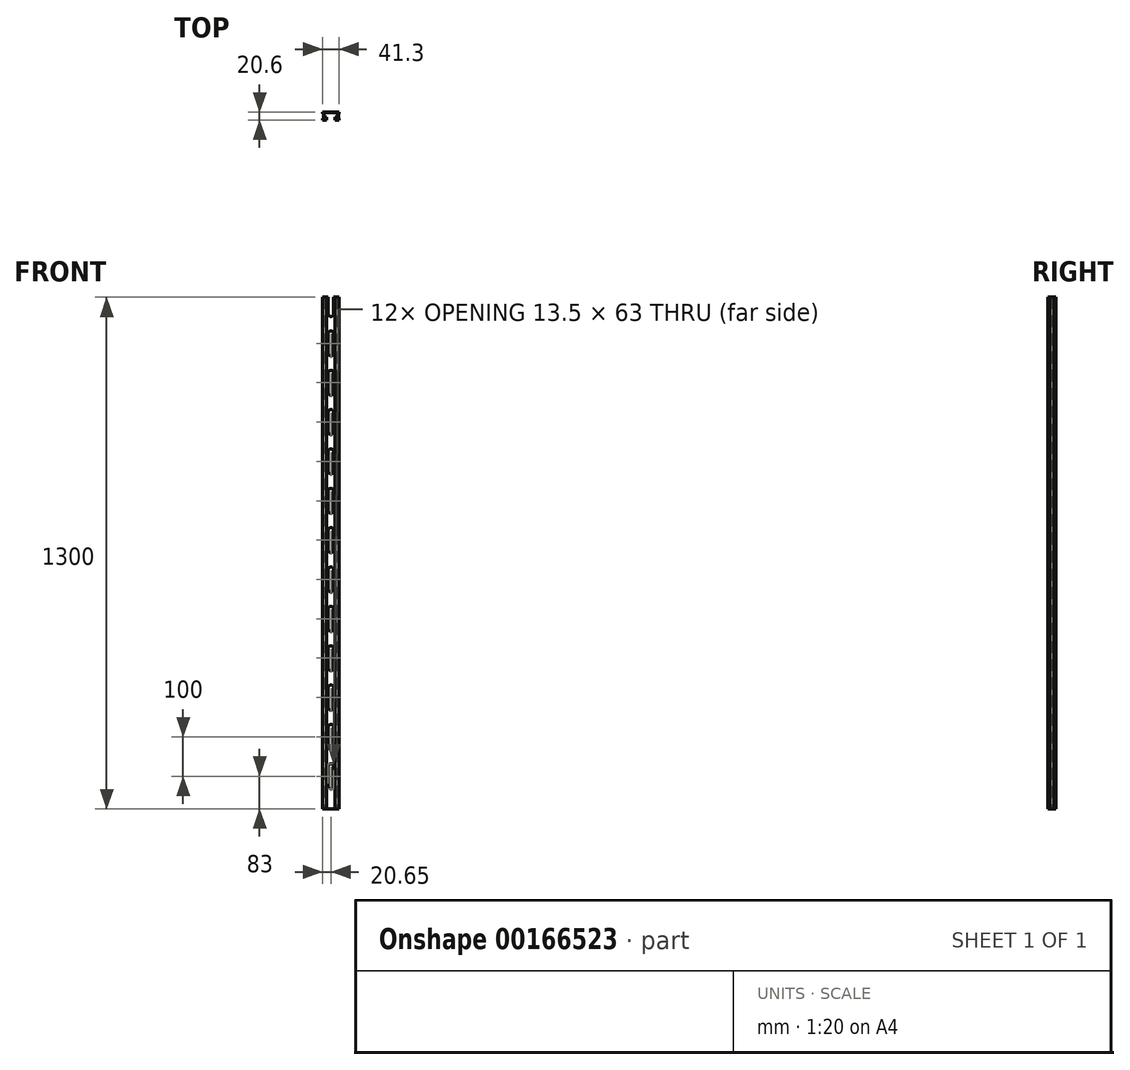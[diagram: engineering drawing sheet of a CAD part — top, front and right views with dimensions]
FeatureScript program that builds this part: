
annotation { "Feature Type Name" : "Feature", "Feature Type Description" : "" }
export const myFeature = defineFeature(function(context is Context, id is Id, definition is map)
    precondition{}
    {
        {
            var Q0;
            Q0=qCreatedBy(makeId("Top.planeOp"),FACE);
            var sketch = newSketch(context, id + "F0", { "sketchPlane" : qUnion([Q0])});
            skPoint(sketch, "E0.middle", {"position": v(0, 0) * mm});
            skLineSegment(sketch, "E1", {"start": v(0, 10.3) * mm, "end": v(-20.65, 10.3) * mm});
            skLineSegment(sketch, "E2", {"start": v(0, 8.3) * mm, "end": v(-18.65, 8.3) * mm});
            skLineSegment(sketch, "E3", {"start": v(-18.65, 8.3) * mm, "end": v(-18.65, 6.8) * mm});
            skLineSegment(sketch, "E4", {"start": v(-18.65, 6.8) * mm, "end": v(-17.15, 6.8) * mm, "construction": true});
            skLineSegment(sketch, "E5", {"start": v(-17.15, 6.8) * mm, "end": v(-17.15, 5.3) * mm, "construction": true});
            skPoint(sketch, "E6.endSnap0", {"position": v(-20.65, 0) * mm});
            skLineSegment(sketch, "E7", {"start": v(-17.15, -5.3) * mm, "end": v(-17.15, -6.8) * mm, "construction": true});
            skLineSegment(sketch, "E8", {"start": v(-17.15, -6.8) * mm, "end": v(-18.65, -6.8) * mm, "construction": true});
            skLineSegment(sketch, "E9", {"start": v(-20.65, 10.3) * mm, "end": v(-20.65, 6.3) * mm});
            skLineSegment(sketch, "E10", {"start": v(-20.65, 6.3) * mm, "end": v(-19.15, 6.3) * mm, "construction": true});
            skLineSegment(sketch, "E11", {"start": v(-20.65, -10.3) * mm, "end": v(-20.65, -6.3) * mm});
            skLineSegment(sketch, "E12", {"start": v(-20.65, -6.3) * mm, "end": v(-19.15, -6.3) * mm, "construction": true});
            skLineSegment(sketch, "E13", {"start": v(-19.15, -6.3) * mm, "end": v(-19.15, -4.8) * mm, "construction": true});
            skLineSegment(sketch, "E14", {"start": v(-19.15, 6.3) * mm, "end": v(-19.15, 4.8) * mm, "construction": true});
            skLineSegment(sketch, "E15", {"start": v(-20.65, 6.3) * mm, "end": v(-19.15, 4.8) * mm});
            skLineSegment(sketch, "E16", {"start": v(-19.15, -4.8) * mm, "end": v(-20.65, -6.3) * mm});
            skLineSegment(sketch, "E17", {"start": v(-19.15, -4.8) * mm, "end": v(-19.15, 4.8) * mm});
            skLineSegment(sketch, "E18", {"start": v(-18.65, -6.8) * mm, "end": v(-17.15, -5.3) * mm});
            skLineSegment(sketch, "E19", {"start": v(-17.15, 5.3) * mm, "end": v(-18.65, 6.8) * mm});
            skLineSegment(sketch, "E20", {"start": v(-17.15, 5.3) * mm, "end": v(-17.15, -5.3) * mm});
            skLineSegment(sketch, "E21", {"start": v(-20.65, -10.3) * mm, "end": v(-11.15, -10.3) * mm});
            skLineSegment(sketch, "E22", {"start": v(-11.15, -10.3) * mm, "end": v(-11.15, -2.8) * mm});
            skLineSegment(sketch, "E23", {"start": v(-11.15, -2.8) * mm, "end": v(-13.15, -2.8) * mm});
            skLineSegment(sketch, "E24", {"start": v(-13.15, -2.8) * mm, "end": v(-13.15, -8.3) * mm});
            skLineSegment(sketch, "E25", {"start": v(-13.15, -8.3) * mm, "end": v(-18.65, -8.3) * mm});
            skLineSegment(sketch, "E26", {"start": v(-18.65, -6.8) * mm, "end": v(-18.65, -8.3) * mm});
            skLineSegment(sketch, "E27.MirrorCS", {"start": v(20.65, -10.3) * mm, "end": v(11.15, -10.3) * mm});
            skLineSegment(sketch, "E28.MirrorCS", {"start": v(11.15, -2.8) * mm, "end": v(13.15, -2.8) * mm});
            skLineSegment(sketch, "E29.MirrorCS", {"start": v(11.15, -10.3) * mm, "end": v(11.15, -2.8) * mm});
            skLineSegment(sketch, "E30.MirrorCS", {"start": v(13.15, -8.3) * mm, "end": v(18.65, -8.3) * mm});
            skLineSegment(sketch, "E31.MirrorCS", {"start": v(13.15, -2.8) * mm, "end": v(13.15, -8.3) * mm});
            skLineSegment(sketch, "E32.MirrorCS", {"start": v(20.65, -10.3) * mm, "end": v(20.65, -6.3) * mm});
            skLineSegment(sketch, "E33.MirrorCS", {"start": v(18.65, -6.8) * mm, "end": v(18.65, -8.3) * mm});
            skLineSegment(sketch, "E34.MirrorCS", {"start": v(18.65, -6.8) * mm, "end": v(17.15, -5.3) * mm});
            skLineSegment(sketch, "E35.MirrorCS", {"start": v(19.15, -4.8) * mm, "end": v(20.65, -6.3) * mm});
            skLineSegment(sketch, "E36.MirrorCS", {"start": v(19.15, -4.8) * mm, "end": v(19.15, 4.8) * mm});
            skLineSegment(sketch, "E37.MirrorCS", {"start": v(17.15, 5.3) * mm, "end": v(17.15, -5.3) * mm});
            skLineSegment(sketch, "E38.MirrorCS", {"start": v(18.65, 8.3) * mm, "end": v(18.65, 6.8) * mm});
            skLineSegment(sketch, "E39.MirrorCS", {"start": v(17.15, 5.3) * mm, "end": v(18.65, 6.8) * mm});
            skLineSegment(sketch, "E40.MirrorCS", {"start": v(20.65, 6.3) * mm, "end": v(19.15, 4.8) * mm});
            skLineSegment(sketch, "E41.MirrorCS", {"start": v(20.65, 10.3) * mm, "end": v(20.65, 6.3) * mm});
            skLineSegment(sketch, "E42.MirrorCS", {"start": v(0, 10.3) * mm, "end": v(20.65, 10.3) * mm});
            skLineSegment(sketch, "E43.MirrorCS", {"start": v(0, 8.3) * mm, "end": v(18.65, 8.3) * mm});
            skSolve(sketch);
        }
        {
            var Q0;
            Q0=makeQuery(id+"F0.imprint","IMPRINT",FACE,{"disambiguationData":[TD([[makeQuery(id+"F0.imprint","IMPRINT",EDGE,{"derivedFrom":sQuery(id+"F0.wireOp",EDGE,"E1")}),1.0]])]});
            extrude(context, id + "F1", {"entities" : qUnion([Q0]), "depth" : 1300 * mm});
        }
        {
            var Q0;
            Q0=makeQuery(id+"F1.opExtrude","SWEPT_FACE",FACE,{"disambiguationData":[OSD([sQuery(id+"F0.wireOp",EDGE,"E1"),sQuery(id+"F0.wireOp",EDGE,"E42.MirrorCS")])]});
            var sketch = newSketch(context, id + "F2", { "sketchPlane" : qUnion([Q0])});
            skLineSegment(sketch, "E44", {"start": v(0, 0) * mm, "end": v(0, 83) * mm, "construction": true});
            skLineSegment(sketch, "E45.bottom", {"start": v(0.5, 51.5) * mm, "end": v(-0.5, 51.5) * mm});
            skLineSegment(sketch, "E45.top", {"start": v(0.5, 114.5) * mm, "end": v(-0.5, 114.5) * mm});
            skLineSegment(sketch, "E45.left", {"start": v(6.75, 57.75) * mm, "end": v(6.75, 108.25) * mm});
            skLineSegment(sketch, "E45.right", {"start": v(-6.75, 57.75) * mm, "end": v(-6.75, 108.25) * mm});
            skPoint(sketch, "E45.middle", {"position": v(0, 83) * mm});
            skPoint(sketch, "E46.visualSharp", {"position": v(-6.75, 114.5) * mm});
            skArc(sketch, "E46.filletArc", {"start": v(-0.5, 114.5) * mm, "mid": v(-4.92, 112.67) * mm, "end": v(-6.75, 108.25) * mm});
            skPoint(sketch, "E47.visualSharp", {"position": v(6.75, 114.5) * mm});
            skArc(sketch, "E47.filletArc", {"start": v(6.75, 108.25) * mm, "mid": v(4.92, 112.67) * mm, "end": v(0.5, 114.5) * mm});
            skPoint(sketch, "E48.visualSharp", {"position": v(6.75, 51.5) * mm});
            skArc(sketch, "E48.filletArc", {"start": v(0.5, 51.5) * mm, "mid": v(4.92, 53.33) * mm, "end": v(6.75, 57.75) * mm});
            skPoint(sketch, "E49.visualSharp", {"position": v(-6.75, 51.5) * mm});
            skArc(sketch, "E49.filletArc", {"start": v(-6.75, 57.75) * mm, "mid": v(-4.92, 53.33) * mm, "end": v(-0.5, 51.5) * mm});
            skLineSegment(sketch, "E50.0.1.0", {"start": v(-6.75, 157.75) * mm, "end": v(-6.75, 208.25) * mm});
            skArc(sketch, "E50.0.1.1", {"start": v(-0.5, 214.5) * mm, "mid": v(-4.92, 212.67) * mm, "end": v(-6.75, 208.25) * mm});
            skArc(sketch, "E50.0.1.2", {"start": v(6.75, 208.25) * mm, "mid": v(4.92, 212.67) * mm, "end": v(0.5, 214.5) * mm});
            skLineSegment(sketch, "E50.0.1.3", {"start": v(0.5, 214.5) * mm, "end": v(-0.5, 214.5) * mm});
            skLineSegment(sketch, "E50.0.1.4", {"start": v(6.75, 157.75) * mm, "end": v(6.75, 208.25) * mm});
            skArc(sketch, "E50.0.1.5", {"start": v(0.5, 151.5) * mm, "mid": v(4.92, 153.33) * mm, "end": v(6.75, 157.75) * mm});
            skLineSegment(sketch, "E50.0.1.6", {"start": v(0.5, 151.5) * mm, "end": v(-0.5, 151.5) * mm});
            skArc(sketch, "E50.0.1.7", {"start": v(-6.75, 157.75) * mm, "mid": v(-4.92, 153.33) * mm, "end": v(-0.5, 151.5) * mm});
            skLineSegment(sketch, "E50.0.2.0", {"start": v(-6.75, 257.75) * mm, "end": v(-6.75, 308.25) * mm});
            skArc(sketch, "E50.0.2.1", {"start": v(-0.5, 314.5) * mm, "mid": v(-4.92, 312.67) * mm, "end": v(-6.75, 308.25) * mm});
            skArc(sketch, "E50.0.2.2", {"start": v(6.75, 308.25) * mm, "mid": v(4.92, 312.67) * mm, "end": v(0.5, 314.5) * mm});
            skLineSegment(sketch, "E50.0.2.3", {"start": v(0.5, 314.5) * mm, "end": v(-0.5, 314.5) * mm});
            skLineSegment(sketch, "E50.0.2.4", {"start": v(6.75, 257.75) * mm, "end": v(6.75, 308.25) * mm});
            skArc(sketch, "E50.0.2.5", {"start": v(0.5, 251.5) * mm, "mid": v(4.92, 253.33) * mm, "end": v(6.75, 257.75) * mm});
            skLineSegment(sketch, "E50.0.2.6", {"start": v(0.5, 251.5) * mm, "end": v(-0.5, 251.5) * mm});
            skArc(sketch, "E50.0.2.7", {"start": v(-6.75, 257.75) * mm, "mid": v(-4.92, 253.33) * mm, "end": v(-0.5, 251.5) * mm});
            skLineSegment(sketch, "E50.0.3.0", {"start": v(-6.75, 357.75) * mm, "end": v(-6.75, 408.25) * mm});
            skArc(sketch, "E50.0.3.1", {"start": v(-0.5, 414.5) * mm, "mid": v(-4.92, 412.67) * mm, "end": v(-6.75, 408.25) * mm});
            skArc(sketch, "E50.0.3.2", {"start": v(6.75, 408.25) * mm, "mid": v(4.92, 412.67) * mm, "end": v(0.5, 414.5) * mm});
            skLineSegment(sketch, "E50.0.3.3", {"start": v(0.5, 414.5) * mm, "end": v(-0.5, 414.5) * mm});
            skLineSegment(sketch, "E50.0.3.4", {"start": v(6.75, 357.75) * mm, "end": v(6.75, 408.25) * mm});
            skArc(sketch, "E50.0.3.5", {"start": v(0.5, 351.5) * mm, "mid": v(4.92, 353.33) * mm, "end": v(6.75, 357.75) * mm});
            skLineSegment(sketch, "E50.0.3.6", {"start": v(0.5, 351.5) * mm, "end": v(-0.5, 351.5) * mm});
            skArc(sketch, "E50.0.3.7", {"start": v(-6.75, 357.75) * mm, "mid": v(-4.92, 353.33) * mm, "end": v(-0.5, 351.5) * mm});
            skLineSegment(sketch, "E50.0.4.0", {"start": v(-6.75, 457.75) * mm, "end": v(-6.75, 508.25) * mm});
            skArc(sketch, "E50.0.4.1", {"start": v(-0.5, 514.5) * mm, "mid": v(-4.92, 512.67) * mm, "end": v(-6.75, 508.25) * mm});
            skArc(sketch, "E50.0.4.2", {"start": v(6.75, 508.25) * mm, "mid": v(4.92, 512.67) * mm, "end": v(0.5, 514.5) * mm});
            skLineSegment(sketch, "E50.0.4.3", {"start": v(0.5, 514.5) * mm, "end": v(-0.5, 514.5) * mm});
            skLineSegment(sketch, "E50.0.4.4", {"start": v(6.75, 457.75) * mm, "end": v(6.75, 508.25) * mm});
            skArc(sketch, "E50.0.4.5", {"start": v(0.5, 451.5) * mm, "mid": v(4.92, 453.33) * mm, "end": v(6.75, 457.75) * mm});
            skLineSegment(sketch, "E50.0.4.6", {"start": v(0.5, 451.5) * mm, "end": v(-0.5, 451.5) * mm});
            skArc(sketch, "E50.0.4.7", {"start": v(-6.75, 457.75) * mm, "mid": v(-4.92, 453.33) * mm, "end": v(-0.5, 451.5) * mm});
            skLineSegment(sketch, "E50.0.5.0", {"start": v(-6.75, 557.75) * mm, "end": v(-6.75, 608.25) * mm});
            skArc(sketch, "E50.0.5.1", {"start": v(-0.5, 614.5) * mm, "mid": v(-4.92, 612.67) * mm, "end": v(-6.75, 608.25) * mm});
            skArc(sketch, "E50.0.5.2", {"start": v(6.75, 608.25) * mm, "mid": v(4.92, 612.67) * mm, "end": v(0.5, 614.5) * mm});
            skLineSegment(sketch, "E50.0.5.3", {"start": v(0.5, 614.5) * mm, "end": v(-0.5, 614.5) * mm});
            skLineSegment(sketch, "E50.0.5.4", {"start": v(6.75, 557.75) * mm, "end": v(6.75, 608.25) * mm});
            skArc(sketch, "E50.0.5.5", {"start": v(0.5, 551.5) * mm, "mid": v(4.92, 553.33) * mm, "end": v(6.75, 557.75) * mm});
            skLineSegment(sketch, "E50.0.5.6", {"start": v(0.5, 551.5) * mm, "end": v(-0.5, 551.5) * mm});
            skArc(sketch, "E50.0.5.7", {"start": v(-6.75, 557.75) * mm, "mid": v(-4.92, 553.33) * mm, "end": v(-0.5, 551.5) * mm});
            skLineSegment(sketch, "E50.0.6.0", {"start": v(-6.75, 657.75) * mm, "end": v(-6.75, 708.25) * mm});
            skArc(sketch, "E50.0.6.1", {"start": v(-0.5, 714.5) * mm, "mid": v(-4.92, 712.67) * mm, "end": v(-6.75, 708.25) * mm});
            skArc(sketch, "E50.0.6.2", {"start": v(6.75, 708.25) * mm, "mid": v(4.92, 712.67) * mm, "end": v(0.5, 714.5) * mm});
            skLineSegment(sketch, "E50.0.6.3", {"start": v(0.5, 714.5) * mm, "end": v(-0.5, 714.5) * mm});
            skLineSegment(sketch, "E50.0.6.4", {"start": v(6.75, 657.75) * mm, "end": v(6.75, 708.25) * mm});
            skArc(sketch, "E50.0.6.5", {"start": v(0.5, 651.5) * mm, "mid": v(4.92, 653.33) * mm, "end": v(6.75, 657.75) * mm});
            skLineSegment(sketch, "E50.0.6.6", {"start": v(0.5, 651.5) * mm, "end": v(-0.5, 651.5) * mm});
            skArc(sketch, "E50.0.6.7", {"start": v(-6.75, 657.75) * mm, "mid": v(-4.92, 653.33) * mm, "end": v(-0.5, 651.5) * mm});
            skLineSegment(sketch, "E50.0.7.0", {"start": v(-6.75, 757.75) * mm, "end": v(-6.75, 808.25) * mm});
            skArc(sketch, "E50.0.7.1", {"start": v(-0.5, 814.5) * mm, "mid": v(-4.92, 812.67) * mm, "end": v(-6.75, 808.25) * mm});
            skArc(sketch, "E50.0.7.2", {"start": v(6.75, 808.25) * mm, "mid": v(4.92, 812.67) * mm, "end": v(0.5, 814.5) * mm});
            skLineSegment(sketch, "E50.0.7.3", {"start": v(0.5, 814.5) * mm, "end": v(-0.5, 814.5) * mm});
            skLineSegment(sketch, "E50.0.7.4", {"start": v(6.75, 757.75) * mm, "end": v(6.75, 808.25) * mm});
            skArc(sketch, "E50.0.7.5", {"start": v(0.5, 751.5) * mm, "mid": v(4.92, 753.33) * mm, "end": v(6.75, 757.75) * mm});
            skLineSegment(sketch, "E50.0.7.6", {"start": v(0.5, 751.5) * mm, "end": v(-0.5, 751.5) * mm});
            skArc(sketch, "E50.0.7.7", {"start": v(-6.75, 757.75) * mm, "mid": v(-4.92, 753.33) * mm, "end": v(-0.5, 751.5) * mm});
            skLineSegment(sketch, "E50.0.8.0", {"start": v(-6.75, 857.75) * mm, "end": v(-6.75, 908.25) * mm});
            skArc(sketch, "E50.0.8.1", {"start": v(-0.5, 914.5) * mm, "mid": v(-4.92, 912.67) * mm, "end": v(-6.75, 908.25) * mm});
            skArc(sketch, "E50.0.8.2", {"start": v(6.75, 908.25) * mm, "mid": v(4.92, 912.67) * mm, "end": v(0.5, 914.5) * mm});
            skLineSegment(sketch, "E50.0.8.3", {"start": v(0.5, 914.5) * mm, "end": v(-0.5, 914.5) * mm});
            skLineSegment(sketch, "E50.0.8.4", {"start": v(6.75, 857.75) * mm, "end": v(6.75, 908.25) * mm});
            skArc(sketch, "E50.0.8.5", {"start": v(0.5, 851.5) * mm, "mid": v(4.92, 853.33) * mm, "end": v(6.75, 857.75) * mm});
            skLineSegment(sketch, "E50.0.8.6", {"start": v(0.5, 851.5) * mm, "end": v(-0.5, 851.5) * mm});
            skArc(sketch, "E50.0.8.7", {"start": v(-6.75, 857.75) * mm, "mid": v(-4.92, 853.33) * mm, "end": v(-0.5, 851.5) * mm});
            skLineSegment(sketch, "E50.0.9.0", {"start": v(-6.75, 957.75) * mm, "end": v(-6.75, 1008.25) * mm});
            skArc(sketch, "E50.0.9.1", {"start": v(-0.5, 1014.5) * mm, "mid": v(-4.92, 1012.67) * mm, "end": v(-6.75, 1008.25) * mm});
            skArc(sketch, "E50.0.9.2", {"start": v(6.75, 1008.25) * mm, "mid": v(4.92, 1012.67) * mm, "end": v(0.5, 1014.5) * mm});
            skLineSegment(sketch, "E50.0.9.3", {"start": v(0.5, 1014.5) * mm, "end": v(-0.5, 1014.5) * mm});
            skLineSegment(sketch, "E50.0.9.4", {"start": v(6.75, 957.75) * mm, "end": v(6.75, 1008.25) * mm});
            skArc(sketch, "E50.0.9.5", {"start": v(0.5, 951.5) * mm, "mid": v(4.92, 953.33) * mm, "end": v(6.75, 957.75) * mm});
            skLineSegment(sketch, "E50.0.9.6", {"start": v(0.5, 951.5) * mm, "end": v(-0.5, 951.5) * mm});
            skArc(sketch, "E50.0.9.7", {"start": v(-6.75, 957.75) * mm, "mid": v(-4.92, 953.33) * mm, "end": v(-0.5, 951.5) * mm});
            skLineSegment(sketch, "E50.0.10.0", {"start": v(-6.75, 1057.75) * mm, "end": v(-6.75, 1108.25) * mm});
            skArc(sketch, "E50.0.10.1", {"start": v(-0.5, 1114.5) * mm, "mid": v(-4.92, 1112.67) * mm, "end": v(-6.75, 1108.25) * mm});
            skArc(sketch, "E50.0.10.2", {"start": v(6.75, 1108.25) * mm, "mid": v(4.92, 1112.67) * mm, "end": v(0.5, 1114.5) * mm});
            skLineSegment(sketch, "E50.0.10.3", {"start": v(0.5, 1114.5) * mm, "end": v(-0.5, 1114.5) * mm});
            skLineSegment(sketch, "E50.0.10.4", {"start": v(6.75, 1057.75) * mm, "end": v(6.75, 1108.25) * mm});
            skArc(sketch, "E50.0.10.5", {"start": v(0.5, 1051.5) * mm, "mid": v(4.92, 1053.33) * mm, "end": v(6.75, 1057.75) * mm});
            skLineSegment(sketch, "E50.0.10.6", {"start": v(0.5, 1051.5) * mm, "end": v(-0.5, 1051.5) * mm});
            skArc(sketch, "E50.0.10.7", {"start": v(-6.75, 1057.75) * mm, "mid": v(-4.92, 1053.33) * mm, "end": v(-0.5, 1051.5) * mm});
            skLineSegment(sketch, "E50.0.11.0", {"start": v(-6.75, 1157.75) * mm, "end": v(-6.75, 1208.25) * mm});
            skArc(sketch, "E50.0.11.1", {"start": v(-0.5, 1214.5) * mm, "mid": v(-4.92, 1212.67) * mm, "end": v(-6.75, 1208.25) * mm});
            skArc(sketch, "E50.0.11.2", {"start": v(6.75, 1208.25) * mm, "mid": v(4.92, 1212.67) * mm, "end": v(0.5, 1214.5) * mm});
            skLineSegment(sketch, "E50.0.11.3", {"start": v(0.5, 1214.5) * mm, "end": v(-0.5, 1214.5) * mm});
            skLineSegment(sketch, "E50.0.11.4", {"start": v(6.75, 1157.75) * mm, "end": v(6.75, 1208.25) * mm});
            skArc(sketch, "E50.0.11.5", {"start": v(0.5, 1151.5) * mm, "mid": v(4.92, 1153.33) * mm, "end": v(6.75, 1157.75) * mm});
            skLineSegment(sketch, "E50.0.11.6", {"start": v(0.5, 1151.5) * mm, "end": v(-0.5, 1151.5) * mm});
            skArc(sketch, "E50.0.11.7", {"start": v(-6.75, 1157.75) * mm, "mid": v(-4.92, 1153.33) * mm, "end": v(-0.5, 1151.5) * mm});
            skLineSegment(sketch, "E50.0.12.0", {"start": v(-6.75, 1257.75) * mm, "end": v(-6.75, 1308.25) * mm});
            skArc(sketch, "E50.0.12.1", {"start": v(-0.5, 1314.5) * mm, "mid": v(-4.92, 1312.67) * mm, "end": v(-6.75, 1308.25) * mm});
            skArc(sketch, "E50.0.12.2", {"start": v(6.75, 1308.25) * mm, "mid": v(4.92, 1312.67) * mm, "end": v(0.5, 1314.5) * mm});
            skLineSegment(sketch, "E50.0.12.3", {"start": v(0.5, 1314.5) * mm, "end": v(-0.5, 1314.5) * mm});
            skLineSegment(sketch, "E50.0.12.4", {"start": v(6.75, 1257.75) * mm, "end": v(6.75, 1308.25) * mm});
            skArc(sketch, "E50.0.12.5", {"start": v(0.5, 1251.5) * mm, "mid": v(4.92, 1253.33) * mm, "end": v(6.75, 1257.75) * mm});
            skLineSegment(sketch, "E50.0.12.6", {"start": v(0.5, 1251.5) * mm, "end": v(-0.5, 1251.5) * mm});
            skArc(sketch, "E50.0.12.7", {"start": v(-6.75, 1257.75) * mm, "mid": v(-4.92, 1253.33) * mm, "end": v(-0.5, 1251.5) * mm});
            skLineSegment(sketch, "E50.0.13.0", {"start": v(-6.75, 1357.75) * mm, "end": v(-6.75, 1408.25) * mm});
            skArc(sketch, "E50.0.13.1", {"start": v(-0.5, 1414.5) * mm, "mid": v(-4.92, 1412.67) * mm, "end": v(-6.75, 1408.25) * mm});
            skArc(sketch, "E50.0.13.2", {"start": v(6.75, 1408.25) * mm, "mid": v(4.92, 1412.67) * mm, "end": v(0.5, 1414.5) * mm});
            skLineSegment(sketch, "E50.0.13.3", {"start": v(0.5, 1414.5) * mm, "end": v(-0.5, 1414.5) * mm});
            skLineSegment(sketch, "E50.0.13.4", {"start": v(6.75, 1357.75) * mm, "end": v(6.75, 1408.25) * mm});
            skArc(sketch, "E50.0.13.5", {"start": v(0.5, 1351.5) * mm, "mid": v(4.92, 1353.33) * mm, "end": v(6.75, 1357.75) * mm});
            skLineSegment(sketch, "E50.0.13.6", {"start": v(0.5, 1351.5) * mm, "end": v(-0.5, 1351.5) * mm});
            skArc(sketch, "E50.0.13.7", {"start": v(-6.75, 1357.75) * mm, "mid": v(-4.92, 1353.33) * mm, "end": v(-0.5, 1351.5) * mm});
            skLineSegment(sketch, "E50.direction1", {"start": v(-0.5, 51.5) * mm, "end": v(24.5, 51.5) * mm, "construction": true});
            skLineSegment(sketch, "E50.direction2", {"start": v(-0.5, 51.5) * mm, "end": v(-0.5, 151.5) * mm, "construction": true});
            skSolve(sketch);
        }
        {
            var Q0;
            Q0=makeQuery(id+"F2.imprint","IMPRINT",FACE,{"disambiguationData":[TD([[makeQuery(id+"F2.imprint","IMPRINT",EDGE,{"derivedFrom":sQuery(id+"F2.wireOp",EDGE,"E45.bottom")}),-1.0]])]});
            var Q1;
            Q1=makeQuery(id+"F2.imprint","IMPRINT",FACE,{"disambiguationData":[TD([[makeQuery(id+"F2.imprint","IMPRINT",EDGE,{"derivedFrom":sQuery(id+"F2.wireOp",EDGE,"E50.0.1.0")}),-1.0]])]});
            var Q2;
            Q2=makeQuery(id+"F2.imprint","IMPRINT",FACE,{"disambiguationData":[TD([[makeQuery(id+"F2.imprint","IMPRINT",EDGE,{"derivedFrom":sQuery(id+"F2.wireOp",EDGE,"E50.0.2.0")}),-1.0]])]});
            var Q3;
            Q3=makeQuery(id+"F2.imprint","IMPRINT",FACE,{"disambiguationData":[TD([[makeQuery(id+"F2.imprint","IMPRINT",EDGE,{"derivedFrom":sQuery(id+"F2.wireOp",EDGE,"E50.0.3.0")}),-1.0]])]});
            var Q4;
            Q4=makeQuery(id+"F2.imprint","IMPRINT",FACE,{"disambiguationData":[TD([[makeQuery(id+"F2.imprint","IMPRINT",EDGE,{"derivedFrom":sQuery(id+"F2.wireOp",EDGE,"E50.0.4.0")}),-1.0]])]});
            var Q5;
            Q5=makeQuery(id+"F2.imprint","IMPRINT",FACE,{"disambiguationData":[TD([[makeQuery(id+"F2.imprint","IMPRINT",EDGE,{"derivedFrom":sQuery(id+"F2.wireOp",EDGE,"E50.0.5.0")}),-1.0]])]});
            var Q6;
            Q6=makeQuery(id+"F2.imprint","IMPRINT",FACE,{"disambiguationData":[TD([[makeQuery(id+"F2.imprint","IMPRINT",EDGE,{"derivedFrom":sQuery(id+"F2.wireOp",EDGE,"E50.0.6.0")}),-1.0]])]});
            var Q7;
            Q7=makeQuery(id+"F2.imprint","IMPRINT",FACE,{"disambiguationData":[TD([[makeQuery(id+"F2.imprint","IMPRINT",EDGE,{"derivedFrom":sQuery(id+"F2.wireOp",EDGE,"E50.0.7.0")}),-1.0]])]});
            var Q8;
            Q8=makeQuery(id+"F2.imprint","IMPRINT",FACE,{"disambiguationData":[TD([[makeQuery(id+"F2.imprint","IMPRINT",EDGE,{"derivedFrom":sQuery(id+"F2.wireOp",EDGE,"E50.0.8.0")}),-1.0]])]});
            var Q9;
            Q9=makeQuery(id+"F2.imprint","IMPRINT",FACE,{"disambiguationData":[TD([[makeQuery(id+"F2.imprint","IMPRINT",EDGE,{"derivedFrom":sQuery(id+"F2.wireOp",EDGE,"E50.0.9.0")}),-1.0]])]});
            var Q10;
            Q10=makeQuery(id+"F2.imprint","IMPRINT",FACE,{"disambiguationData":[TD([[makeQuery(id+"F2.imprint","IMPRINT",EDGE,{"derivedFrom":sQuery(id+"F2.wireOp",EDGE,"E50.0.10.0")}),-1.0]])]});
            var Q11;
            Q11=makeQuery(id+"F2.imprint","IMPRINT",FACE,{"disambiguationData":[TD([[makeQuery(id+"F2.imprint","IMPRINT",EDGE,{"derivedFrom":sQuery(id+"F2.wireOp",EDGE,"E50.0.11.0")}),-1.0]])]});
            var Q12;
            Q12=makeQuery(id+"F2.imprint","IMPRINT",FACE,{"disambiguationData":[TD([[makeQuery(id+"F2.imprint","IMPRINT",EDGE,{"derivedFrom":sQuery(id+"F2.wireOp",EDGE,"E50.0.12.0")}),-1.0]])]});
            extrude(context, id + "F3", {"entities" : qUnion([Q0, Q1, Q2, Q3, Q4, Q5, Q6, Q7, Q8, Q9, Q10, Q11, Q12]), "operationType" : NewBodyOperationType.REMOVE, "oppositeDirection" : true, "depth" : 25 * mm});
        }
    });
